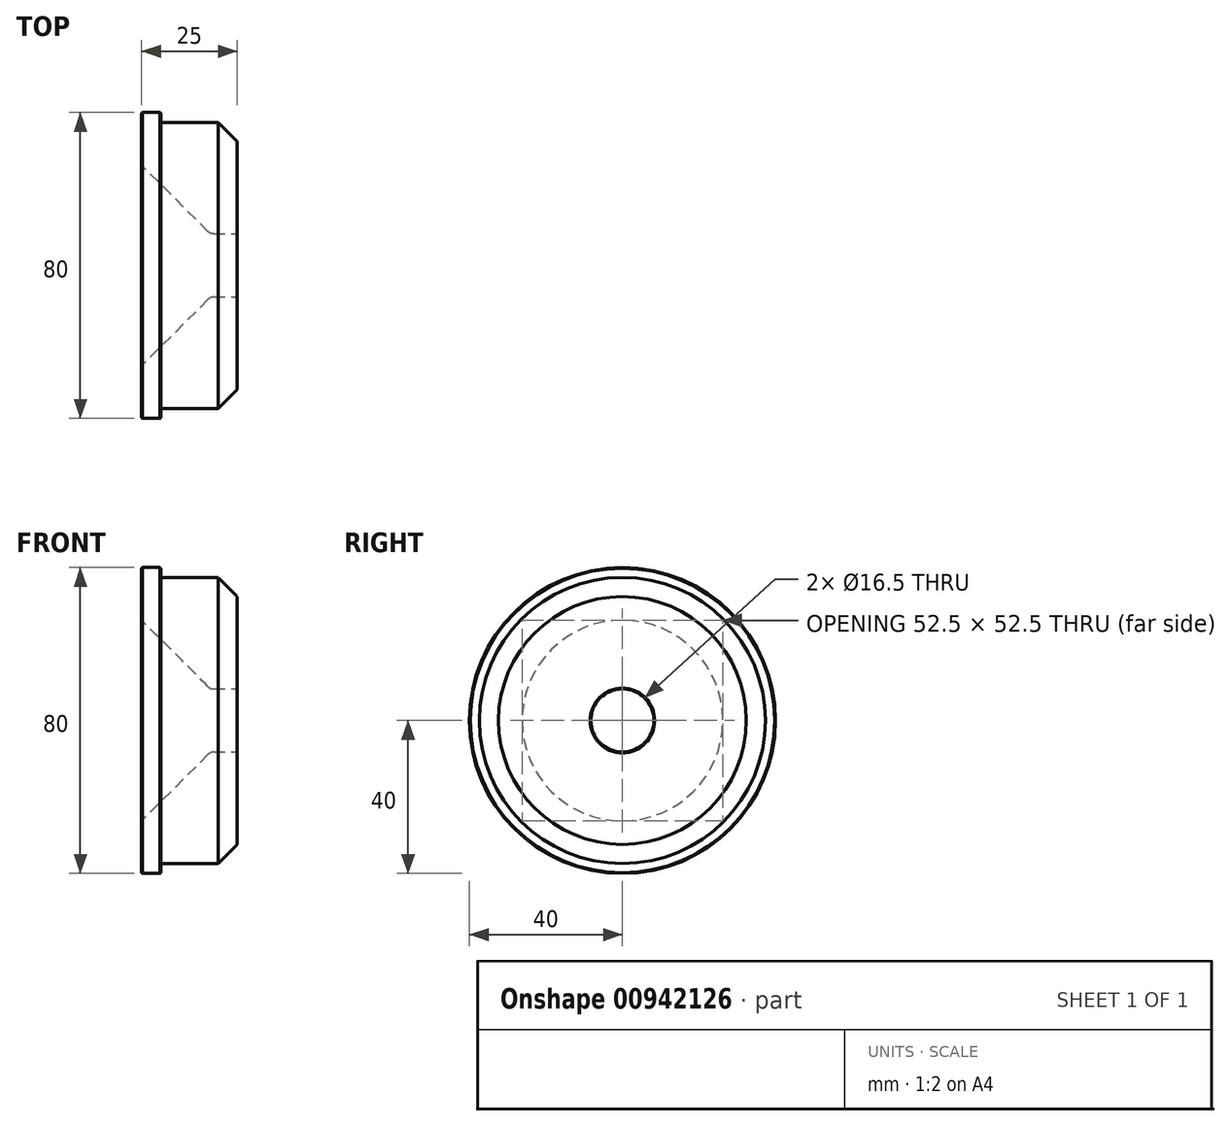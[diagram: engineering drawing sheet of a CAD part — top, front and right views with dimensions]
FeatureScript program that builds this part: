
annotation { "Feature Type Name" : "Feature", "Feature Type Description" : "" }
export const myFeature = defineFeature(function(context is Context, id is Id, definition is map)
    precondition{}
    {
        {
            var Q0;
            Q0=qCreatedBy(makeId("Front.planeOp"),FACE);
            var sketch = newSketch(context, id + "F0", { "sketchPlane" : qUnion([Q0])});
            skLineSegment(sketch, "E0", {"start": v(0, 8.25) * mm, "end": v(0, 40) * mm});
            skLineSegment(sketch, "E1", {"start": v(0, 40) * mm, "end": v(5, 40) * mm});
            skLineSegment(sketch, "E2", {"start": v(5, 40) * mm, "end": v(5, 37.4) * mm});
            skLineSegment(sketch, "E3", {"start": v(5, 37.4) * mm, "end": v(25, 37.4) * mm});
            skLineSegment(sketch, "E4", {"start": v(25, 37.4) * mm, "end": v(25, 8.25) * mm});
            skLineSegment(sketch, "E5", {"start": v(0, 8.25) * mm, "end": v(25, 8.25) * mm});
            skPoint(sketch, "E6.orphan", {"position": v(25, 0) * mm});
            skLineSegment(sketch, "E7", {"start": v(18, 8.25) * mm, "end": v(0, 26.25) * mm});
            skLineSegment(sketch, "E8", {"start": v(25, 0) * mm, "end": v(0, 0) * mm});
            skSolve(sketch);
        }
        {
            var Q0;
            {var subQ0=sQuery(id+"F0.wireOp",EDGE,"E1");Q0=makeQuery(id+"F0.imprint","IMPRINT",FACE,{"disambiguationData":[TD([[makeQuery(id+"F0.imprint","IMPRINT",EDGE,{"derivedFrom":subQ0}),-1.0]])]});}
            var Q1;
            Q1=sQuery(id+"F0.wireOp",EDGE,"E8");
            revolve(context, id + "F1", {"surfaceOperationType" : NewSurfaceOperationType.NEW, "entities" : qUnion([Q0]), "axis" : qUnion([Q1]), "revolveType" : RevolveType.FULL});
        }
        {
            var Q0;
            Q0=makeQuery(id+"F1.opRevolve","SWEPT_EDGE",EDGE,{"disambiguationData":[OSD([sQuery(id+"F0.wireOp",EDGE,"E3"),sQuery(id+"F0.wireOp",EDGE,"E4")])]});
            chamfer(context, id + "F2", {"entities" : qUnion([Q0]), "width" : 5 * mm, "tangentPropagation" : true});
        }
        {
            var Q0;
            Q0=makeQuery(id+"F1.opRevolve","SWEPT_EDGE",EDGE,{"disambiguationData":[OSD([sQuery(id+"F0.wireOp",EDGE,"E4"),sQuery(id+"F0.wireOp",EDGE,"E5")])]});
            var Q1;
            Q1=makeQuery(id+"F1.opRevolve","SWEPT_EDGE",EDGE,{"disambiguationData":[OSD([sQuery(id+"F0.wireOp",EDGE,"E1"),sQuery(id+"F0.wireOp",EDGE,"E2")])]});
            var Q2;
            Q2=makeQuery(id+"F1.opRevolve","SWEPT_EDGE",EDGE,{"disambiguationData":[OSD([sQuery(id+"F0.wireOp",EDGE,"E0"),sQuery(id+"F0.wireOp",EDGE,"E1")])]});
            chamfer(context, id + "F3", {"entities" : qUnion([Q0, Q1, Q2]), "width" : 0.2 * mm, "tangentPropagation" : true});
        }
        {
            var Q0;
            Q0=makeQuery(id+"F1.opRevolve","SWEPT_EDGE",EDGE,{"disambiguationData":[OSD([sQuery(id+"F0.wireOp",EDGE,"E5"),sQuery(id+"F0.wireOp",EDGE,"E7")])]});
            fillet(context, id + "F4", {"entities" : qUnion([Q0]), "radius" : 2 * mm, "tangentPropagation" : true, "allowEdgeOverflow" : false});
        }
    });
